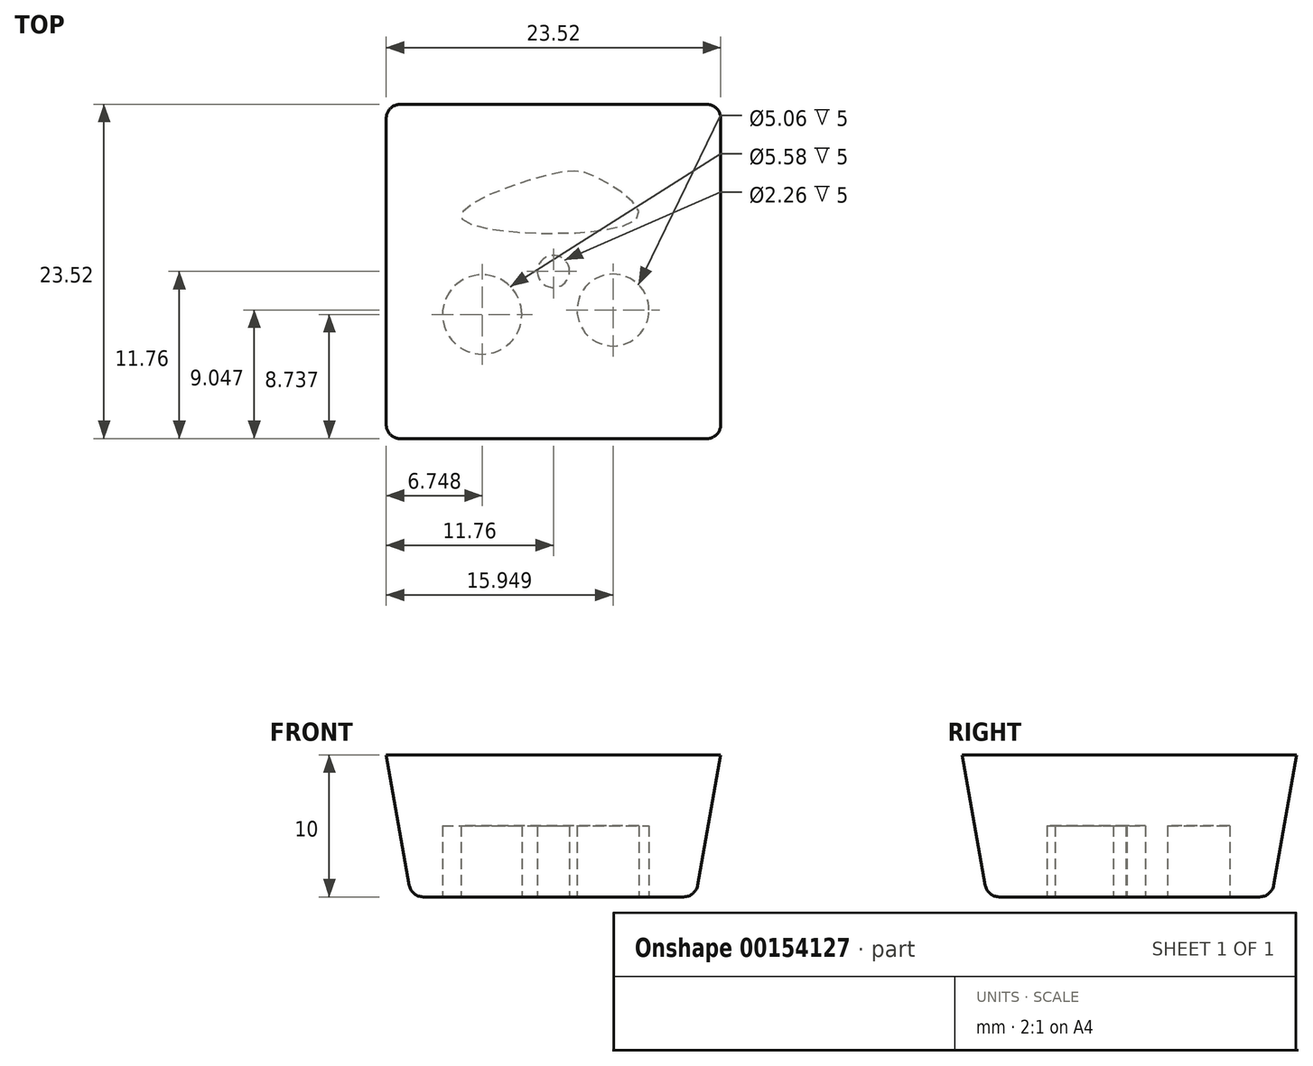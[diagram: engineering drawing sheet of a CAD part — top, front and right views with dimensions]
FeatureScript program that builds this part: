
annotation { "Feature Type Name" : "Feature", "Feature Type Description" : "" }
export const myFeature = defineFeature(function(context is Context, id is Id, definition is map)
    precondition{}
    {
        {
            var Q0;
            Q0=qCreatedBy(makeId("Top.planeOp"),FACE);
            var sketch = newSketch(context, id + "F0", { "sketchPlane" : qUnion([Q0])});
            skLineSegment(sketch, "E0.bottom", {"start": v(-10, -10) * mm, "end": v(10, -10) * mm});
            skLineSegment(sketch, "E0.top", {"start": v(-10, 10) * mm, "end": v(10, 10) * mm});
            skLineSegment(sketch, "E0.left", {"start": v(-10, -10) * mm, "end": v(-10, 10) * mm});
            skLineSegment(sketch, "E0.right", {"start": v(10, -10) * mm, "end": v(10, 10) * mm});
            skPoint(sketch, "E0.middle", {"position": v(0, 0) * mm});
            skSolve(sketch);
        }
        {
            var Q0;
            Q0=makeQuery(id+"F0.imprint","IMPRINT",FACE,{"disambiguationData":[TD([[makeQuery(id+"F0.imprint","IMPRINT",EDGE,{"derivedFrom":sQuery(id+"F0.wireOp",EDGE,"E0.bottom")}),1.0]])]});
            extrude(context, id + "F1", {"entities" : qUnion([Q0]), "depth" : 10 * mm, "hasDraft" : true, "draftAngle" : 10 * degree});
        }
        {
            var Q0;
            Q0=makeQuery(id+"F1.opExtrude","SWEPT_EDGE",EDGE,{"disambiguationData":[OSD([sQuery(id+"F0.wireOp",EDGE,"E0.bottom"),sQuery(id+"F0.wireOp",EDGE,"E0.left")])]});
            var Q1;
            Q1=makeQuery(id+"F1.opExtrude","CAP_EDGE",EDGE,{"disambiguationData":[OSD([sQuery(id+"F0.wireOp",EDGE,"E0.bottom")])],"isStart":true});
            var Q2;
            Q2=makeQuery(id+"F1.opExtrude","CAP_EDGE",EDGE,{"disambiguationData":[OSD([sQuery(id+"F0.wireOp",EDGE,"E0.right")])],"isStart":true});
            var Q3;
            Q3=makeQuery(id+"F1.opExtrude","SWEPT_EDGE",EDGE,{"disambiguationData":[OSD([sQuery(id+"F0.wireOp",EDGE,"E0.bottom"),sQuery(id+"F0.wireOp",EDGE,"E0.right")])]});
            var Q4;
            Q4=makeQuery(id+"F1.opExtrude","SWEPT_EDGE",EDGE,{"disambiguationData":[OSD([sQuery(id+"F0.wireOp",EDGE,"E0.top"),sQuery(id+"F0.wireOp",EDGE,"E0.right")])]});
            var Q5;
            Q5=makeQuery(id+"F1.opExtrude","SWEPT_EDGE",EDGE,{"disambiguationData":[OSD([sQuery(id+"F0.wireOp",EDGE,"E0.top"),sQuery(id+"F0.wireOp",EDGE,"E0.left")])]});
            var Q6;
            Q6=makeQuery(id+"F1.opExtrude","CAP_EDGE",EDGE,{"disambiguationData":[OSD([sQuery(id+"F0.wireOp",EDGE,"E0.left")])],"isStart":true});
            var Q7;
            Q7=makeQuery(id+"F1.opExtrude","CAP_EDGE",EDGE,{"disambiguationData":[OSD([sQuery(id+"F0.wireOp",EDGE,"E0.top")])],"isStart":true});
            fillet(context, id + "F2", {"entities" : qUnion([Q0, Q1, Q2, Q3, Q4, Q5, Q6, Q7]), "radius" : 1 * mm, "tangentPropagation" : true, "allowEdgeOverflow" : false});
        }
        {
            var Q0;
            Q0=makeQuery(id+"F1.opExtrude","CAP_FACE",FACE,{"disambiguationData":[OSD([sQuery(id+"F0.wireOp",EDGE,"E0.bottom"),sQuery(id+"F0.wireOp",EDGE,"E0.top"),sQuery(id+"F0.wireOp",EDGE,"E0.left"),sQuery(id+"F0.wireOp",EDGE,"E0.right")])],"isStart":true});
            var sketch = newSketch(context, id + "F3", { "sketchPlane" : qUnion([Q0])});
            skCircle(sketch, "E1", {"center": v(-5.01, 3.02) * mm, "radius": 2.8 * mm});
            skCircle(sketch, "E2", {"center": v(4.19, 2.71) * mm, "radius": 2.53 * mm});
            skCircle(sketch, "E3", {"center": v(0, 0) * mm, "radius": 0.81 * mm});
            skSolve(sketch);
        }
        {
            var Q0;
            Q0=makeQuery(id+"F3.imprint","IMPRINT",FACE,{"disambiguationData":[TD([[makeQuery(id+"F3.imprint","IMPRINT",EDGE,{"derivedFrom":sQuery(id+"F3.wireOp",EDGE,"E1")}),-1.0]])]});
            var sketch = newSketch(context, id + "F4", { "sketchPlane" : qUnion([Q0])});
            skFitSpline(sketch, "E4", {"points": [v(-6.43, -3.7) * mm, v(5.87, -3.7) * mm, v(3.3, -6.49) * mm, v(-0.37, -6.8) * mm, v(-6.43, -3.7) * mm]});
            skSolve(sketch);
        }
        {
            var Q0;
            Q0=makeQuery(id+"F3.imprint","IMPRINT",FACE,{"disambiguationData":[TD([[makeQuery(id+"F3.imprint","IMPRINT",EDGE,{"derivedFrom":sQuery(id+"F3.wireOp",EDGE,"E1")}),1.0]])]});
            var Q1;
            Q1=makeQuery(id+"F3.imprint","IMPRINT",FACE,{"disambiguationData":[TD([[makeQuery(id+"F3.imprint","IMPRINT",EDGE,{"derivedFrom":sQuery(id+"F3.wireOp",EDGE,"E2")}),1.0]])]});
            extrude(context, id + "F5", {"entities" : qUnion([Q0, Q1]), "operationType" : NewBodyOperationType.REMOVE, "oppositeDirection" : true, "depth" : 5 * mm});
        }
        {
            var Q0;
            Q0=makeQuery(id+"F4.imprint","IMPRINT",FACE,{"disambiguationData":[TD([[makeQuery(id+"F4.imprint","IMPRINT",EDGE,{"derivedFrom":makeQuery(id+"F3.imprint","IMPRINT",EDGE,{"derivedFrom":sQuery(id+"F3.wireOp",EDGE,"E3")})}),1.0]])]});
            var sketch = newSketch(context, id + "F6", { "sketchPlane" : qUnion([Q0])});
            skCircle(sketch, "E5", {"center": v(0, 0) * mm, "radius": 1.13 * mm});
            skSolve(sketch);
        }
        {
            var Q0;
            Q0=makeQuery(id+"F6.imprint","IMPRINT",FACE,{"disambiguationData":[TD([[makeQuery(id+"F6.imprint","IMPRINT",EDGE,{"derivedFrom":sQuery(id+"F6.wireOp",EDGE,"E5")}),1.0]])]});
            extrude(context, id + "F7", {"entities" : qUnion([Q0]), "operationType" : NewBodyOperationType.REMOVE, "oppositeDirection" : true, "depth" : 5 * mm});
        }
        {
            var Q0;
            Q0=makeQuery(id+"F4.imprint","IMPRINT",FACE,{"disambiguationData":[TD([[makeQuery(id+"F4.imprint","IMPRINT",EDGE,{"derivedFrom":sQuery(id+"F4.wireOp",EDGE,"E4")}),-1.0]])]});
            extrude(context, id + "F8", {"entities" : qUnion([Q0]), "operationType" : NewBodyOperationType.REMOVE, "oppositeDirection" : true, "depth" : 5 * mm});
        }
        {
            var Q0;
            Q0=makeQuery(id+"F7.boolean.opBoolean","SPLIT",FACE,{"disambiguationData":[TD([makeQuery(id+"F7.opExtrude","SWEPT_FACE",FACE,{"disambiguationData":[OSD([sQuery(id+"F3.wireOp",EDGE,"E3")])]})])],"derivedFrom":makeQuery(id+"F1.opExtrude","CAP_FACE",FACE,{"disambiguationData":[OSD([sQuery(id+"F0.wireOp",EDGE,"E0.bottom"),sQuery(id+"F0.wireOp",EDGE,"E0.top"),sQuery(id+"F0.wireOp",EDGE,"E0.left"),sQuery(id+"F0.wireOp",EDGE,"E0.right")])],"isStart":true})});
            extrude(context, id + "F9", {"entities" : qUnion([Q0]), "operationType" : NewBodyOperationType.REMOVE, "oppositeDirection" : true, "depth" : 5 * mm});
        }
    });
